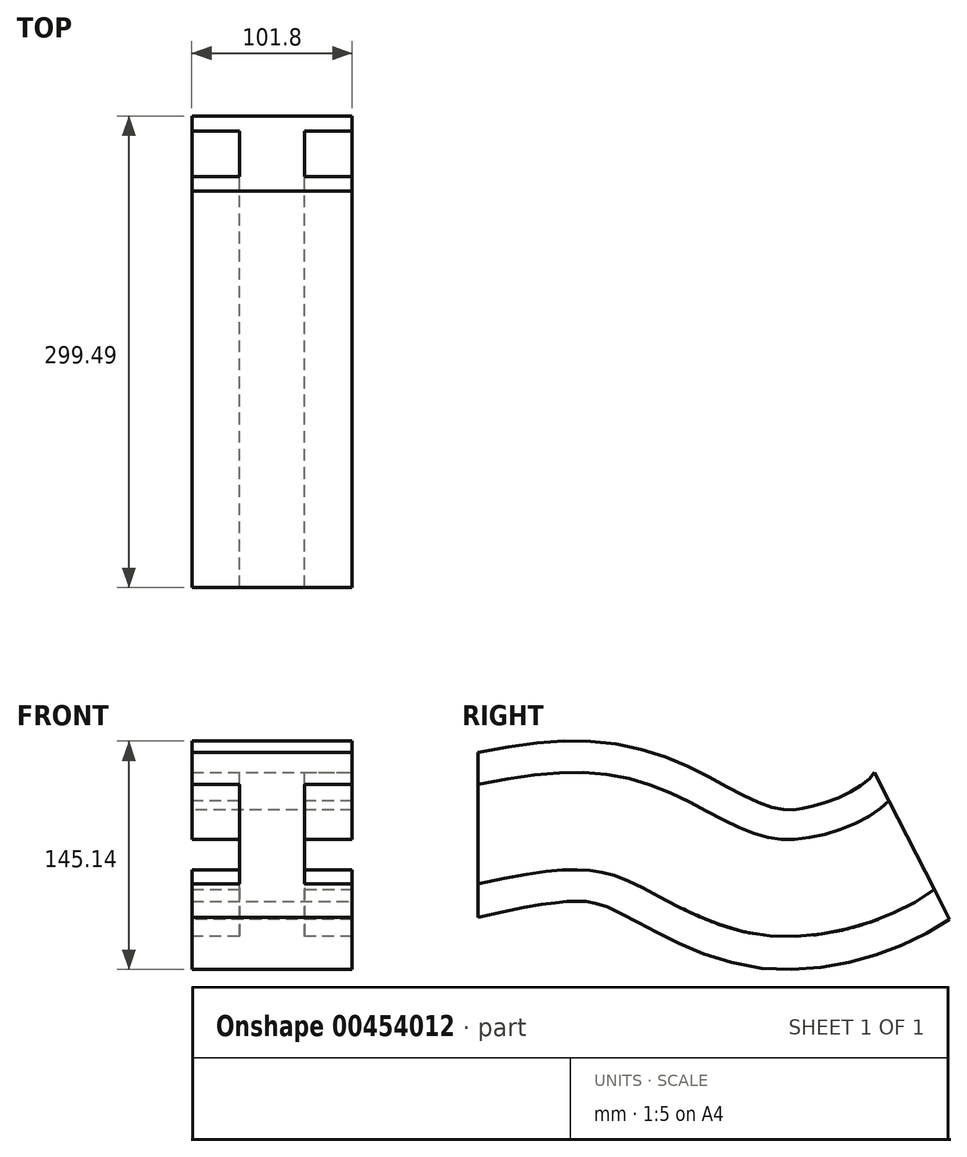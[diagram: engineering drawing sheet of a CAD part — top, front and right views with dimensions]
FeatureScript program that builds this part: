
annotation { "Feature Type Name" : "Feature", "Feature Type Description" : "" }
export const myFeature = defineFeature(function(context is Context, id is Id, definition is map)
    precondition{}
    {
        {
            var Q0;
            Q0=qCreatedBy(makeId("Front.planeOp"),FACE);
            var sketch = newSketch(context, id + "F0", { "sketchPlane" : qUnion([Q0])});
            skLineSegment(sketch, "E0", {"start": v(-48.58, 52.72) * mm, "end": v(51.23, 52.72) * mm});
            skLineSegment(sketch, "E1", {"start": v(51.23, 52.72) * mm, "end": v(51.23, 32.5) * mm});
            skLineSegment(sketch, "E2", {"start": v(51.23, 32.5) * mm, "end": v(21.06, 32.5) * mm});
            skLineSegment(sketch, "E3", {"start": v(21.06, 32.5) * mm, "end": v(21.06, -30.84) * mm});
            skLineSegment(sketch, "E4", {"start": v(21.06, -30.84) * mm, "end": v(51.23, -30.84) * mm});
            skLineSegment(sketch, "E5", {"start": v(51.23, -30.84) * mm, "end": v(51.23, -52.06) * mm});
            skLineSegment(sketch, "E6", {"start": v(51.23, -52.06) * mm, "end": v(-50.57, -52.06) * mm});
            skLineSegment(sketch, "E7", {"start": v(-50.57, -52.06) * mm, "end": v(-50.57, -30.84) * mm});
            skLineSegment(sketch, "E8", {"start": v(-50.57, -30.84) * mm, "end": v(-20.4, -30.84) * mm});
            skLineSegment(sketch, "E9", {"start": v(-20.4, -30.84) * mm, "end": v(-20.4, 32.5) * mm});
            skLineSegment(sketch, "E10", {"start": v(-20.4, 32.5) * mm, "end": v(-50.57, 32.5) * mm});
            skLineSegment(sketch, "E11", {"start": v(-50.57, 32.5) * mm, "end": v(-50.57, 52.72) * mm});
            skLineSegment(sketch, "E12", {"start": v(-50.57, 52.72) * mm, "end": v(-48.58, 52.72) * mm});
            skSolve(sketch);
        }
        {
            var Q0;
            Q0=qCreatedBy(makeId("Right.planeOp"),FACE);
            var sketch = newSketch(context, id + "F1", { "sketchPlane" : qUnion([Q0])});
            skFitSpline(sketch, "E13", {"points": [v(0, 0) * mm, v(103.97, 0) * mm, v(184.9, -33.25) * mm, v(275.76, -6.98) * mm], "startDerivative": vector(425.83, 92.75) * mm, "endDerivative": vector(189.61, 155.77) * mm});
            skSolve(sketch);
        }
        {
            var Q0;
            Q0 = qSketchRegion(id + "F0", true);
            var Q1;
            Q1=sQuery(id+"F1.wireOp",EDGE,"E13");
            sweep(context, id + "F2", {"profiles" : qUnion([Q0]), "path" : qUnion([Q1])});
        }
    });
